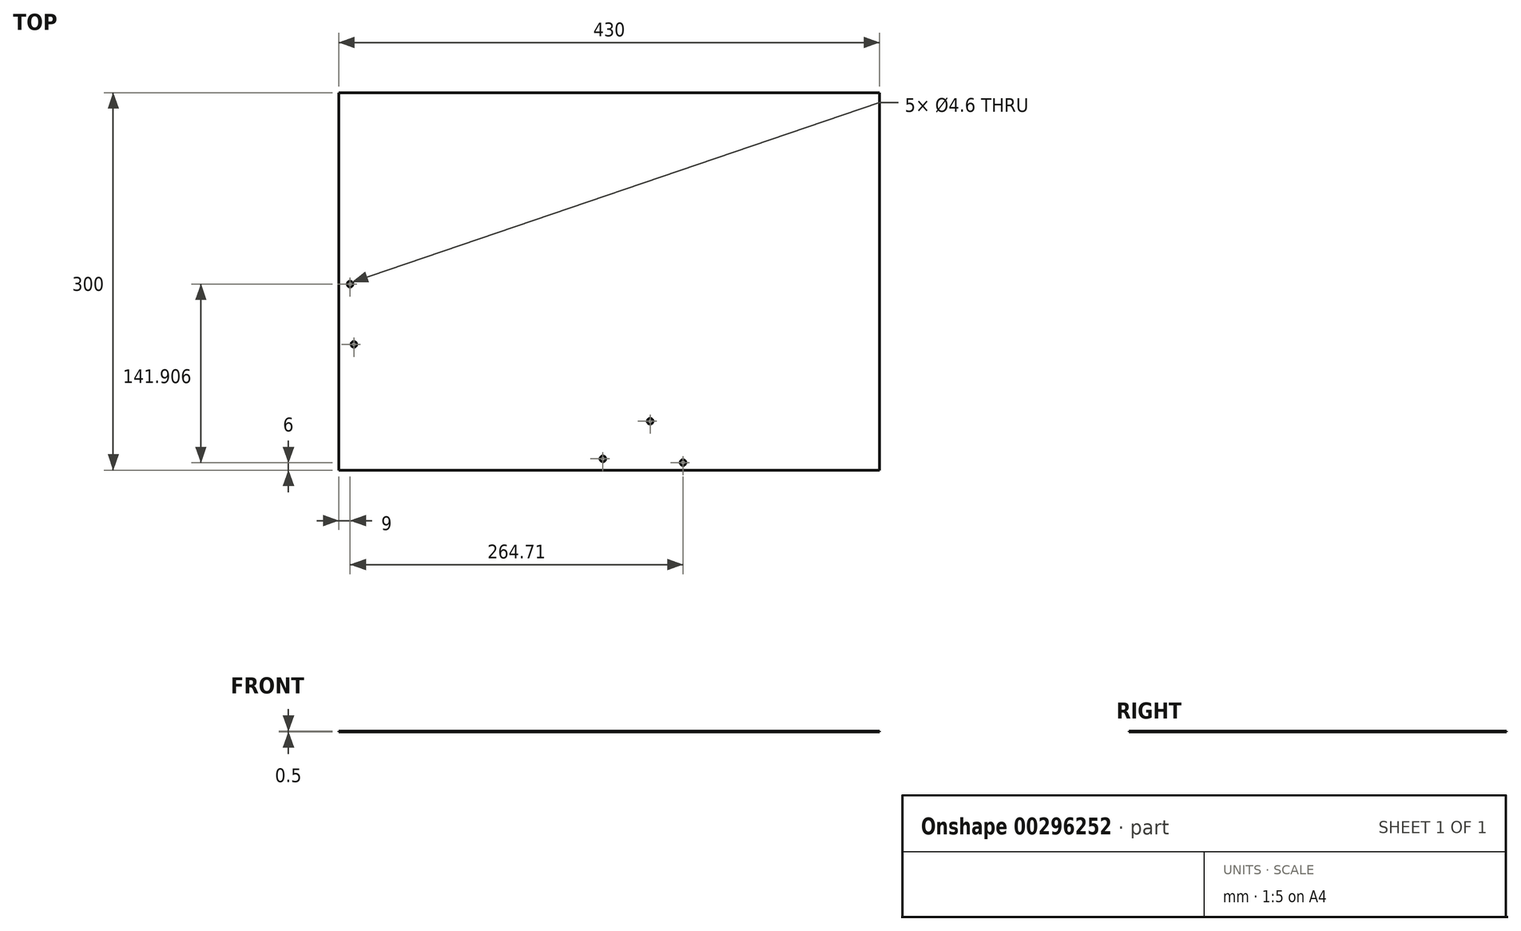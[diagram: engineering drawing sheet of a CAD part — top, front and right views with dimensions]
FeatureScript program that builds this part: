
annotation { "Feature Type Name" : "Feature", "Feature Type Description" : "" }
export const myFeature = defineFeature(function(context is Context, id is Id, definition is map)
    precondition{}
    {
        {
            var Q0;
            Q0=qCreatedBy(makeId("Top.planeOp"),FACE);
            var sketch = newSketch(context, id + "F0", { "sketchPlane" : qUnion([Q0])});
            skLineSegment(sketch, "E0.bottom", {"start": v(0, 0) * mm, "end": v(430, 0) * mm});
            skLineSegment(sketch, "E0.top", {"start": v(0, 300) * mm, "end": v(430, 300) * mm});
            skLineSegment(sketch, "E0.left", {"start": v(0, 0) * mm, "end": v(0, 300) * mm});
            skLineSegment(sketch, "E0.right", {"start": v(430, 0) * mm, "end": v(430, 300) * mm});
            skCircle(sketch, "E1", {"center": v(273.71, 6) * mm, "radius": 2.3 * mm});
            skCircle(sketch, "E2", {"center": v(210, 9) * mm, "radius": 2.3 * mm});
            skCircle(sketch, "E3", {"center": v(247.57, 38.87) * mm, "radius": 2.3 * mm});
            skCircle(sketch, "E4", {"center": v(12, 100) * mm, "radius": 2.3 * mm});
            skCircle(sketch, "E5", {"center": v(9, 147.9) * mm, "radius": 2.3 * mm});
            skLineSegment(sketch, "E6", {"start": v(210, 9) * mm, "end": v(247.57, 38.87) * mm, "construction": true});
            skLineSegment(sketch, "E7", {"start": v(247.57, 38.87) * mm, "end": v(273.71, 6) * mm, "construction": true});
            skLineSegment(sketch, "E8", {"start": v(9, 147.9) * mm, "end": v(12, 100) * mm, "construction": true});
            skSolve(sketch);
        }
        {
            var Q0;
            Q0=makeQuery(id+"F0.imprint","IMPRINT",FACE,{"disambiguationData":[TD([[makeQuery(id+"F0.imprint","IMPRINT",EDGE,{"derivedFrom":sQuery(id+"F0.wireOp",EDGE,"E0.bottom")}),1.0]])]});
            extrude(context, id + "F1", {"entities" : qUnion([Q0]), "flatOperationType" : FlatOperationType.REMOVE, "offsetDistance" : 25 * mm, "depth" : 0.5 * mm, "domain" : OperationDomain.MODEL});
        }
    });
